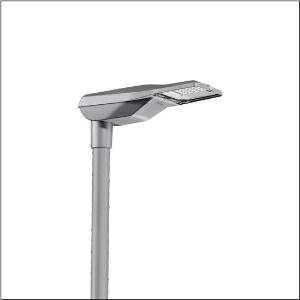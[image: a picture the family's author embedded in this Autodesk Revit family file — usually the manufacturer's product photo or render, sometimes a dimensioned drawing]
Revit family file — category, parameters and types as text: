
# Revit family: streetlight_sl_21_iq_micro___stw1_0a_5xe1e21d08cb_e74e
name_source: partatom
category: Lighting Fixtures
units: mm (PartAtom-declared; Revit-internal decimal feet)

## family parameters
Cut with Voids When Loaded = No
Host = Face
Light Source = No
Part Type = Normal
Room Calculation Point = No
Round Connector Dimension = Use Diameter
Shared = No

## types (1)
- --- (1 x LED, 2380 lm, 19.4 W, 2200K)
    Apparent Load = 19 VA
    CIE Flux Codes = 38 75 98 100 100
    Color Rendering = 70
    Color Temperature = 2200K
    Default Elevation = 1800 mm
    Description = Streetlight SL 21 iQ micro, mast luminaire, primary light control with lens, of PMMA, primary optical cover: cover, of toughened safety glass, transparent, light distribution: STW1.0a, light emission: direct distribution, primary light characteristic: asymmetric, installation type: post-top, side-entry, LED, High Power LED, rated luminous flux: 2.380lm, luminous efficacy: 123lm/W, light colour: 722, colour temperature: 2200K, control: Auto-Match, Temp-Guard, Lumen-Switch, Night-Set, Smart-Wire, Light-Fading, Desk-Remote (wireless, voltage-free reading and setting of iQ features in the workshop via application-optimized NFC function/RFID function), optimised constant luminous flux control (CLO 2.0), presetting dimming linear, mains connection: 220..240V, AC, 50/60Hz, start of lifetime: 19W, end of service life: 20W, reduction: 10W, luminaire housing, of diecast aluminium, powder-coated, Siteco® metallic grey (DB 702S), corrosivity category C5 mid according to DIN EN ISO 12944, please order mast flange separately, inclination adjustable: 0°, 5°, 10°, 15°, sealing non-destructively replaceable, multi-level sealing system, length: 528mm, width: 235mm, height: 110mm, mast flange for spigot size: 42mm (side-entry): 5XC10008XM4, 60/48mm (side-entry/post-top): 5XC10108XM2, 76/60mm (side-entry/post-top): 5XC10108XM1, protection rating (complete): IP66, insulation class (complete): insulation class II (safety insulation), certification: CE, ENEC, ENEC+, VDE, impact resistance: IK09, permissible operating ambient temperature for outdoor applications: -40..+50°C, standard-compliant lighting for roads and squares, packaging unit: 1 piece

Light Distribution: STW1.0a
    Height = 110 mm
    Lamp = 1 x LED
    Lamp Light Flux = 2380 lm
    Lamp Power = 19.4 W
    Lamp count = 1
    Length = 528 mm
    Luminous efficacy = 123 lm/W
    Manufacturer = Siteco
    ModVariant = No
    Model = 5XE1E21D08CB
    Number of Poles = 1
    OnlyDefault = Yes
    Power Factor = 1
    Product Name = Streetlight SL 21 iQ micro | STW1.0a
    Product group = mast luminaire | pylon top
    ProductGroupID = 6100
    Protection Class = Protection class II
    Protection Degree = IP 66
    RLX_Detail_Level = 1
    RLX_Emergency_Light_Flux = 0 lm
    RLX_Emergency_Type = 0
    RLX_Emergency_Type_DB = No
    RlxData = <blob elided: 98597 chars, md5=6246e8f9>
    Socket = socket
    Standby Power = 0 W
    System Light Flux = 2380 lm
    System Power = 19 W
    Type Comments = factory setting: luminous flux: 100 % | dim-lin: 254 | 387 mA
    Type Image = l_1006881.jpg
    URL = http://relux.com
    VarID = @adj_088337
    Voltage = 0 V
    Weight = 0.00 kg
    Width = 235 mm

## geometry (parser evidence)
native form markers: Blend x4, Sweep x11
no freeform markers — native parametric forms only
